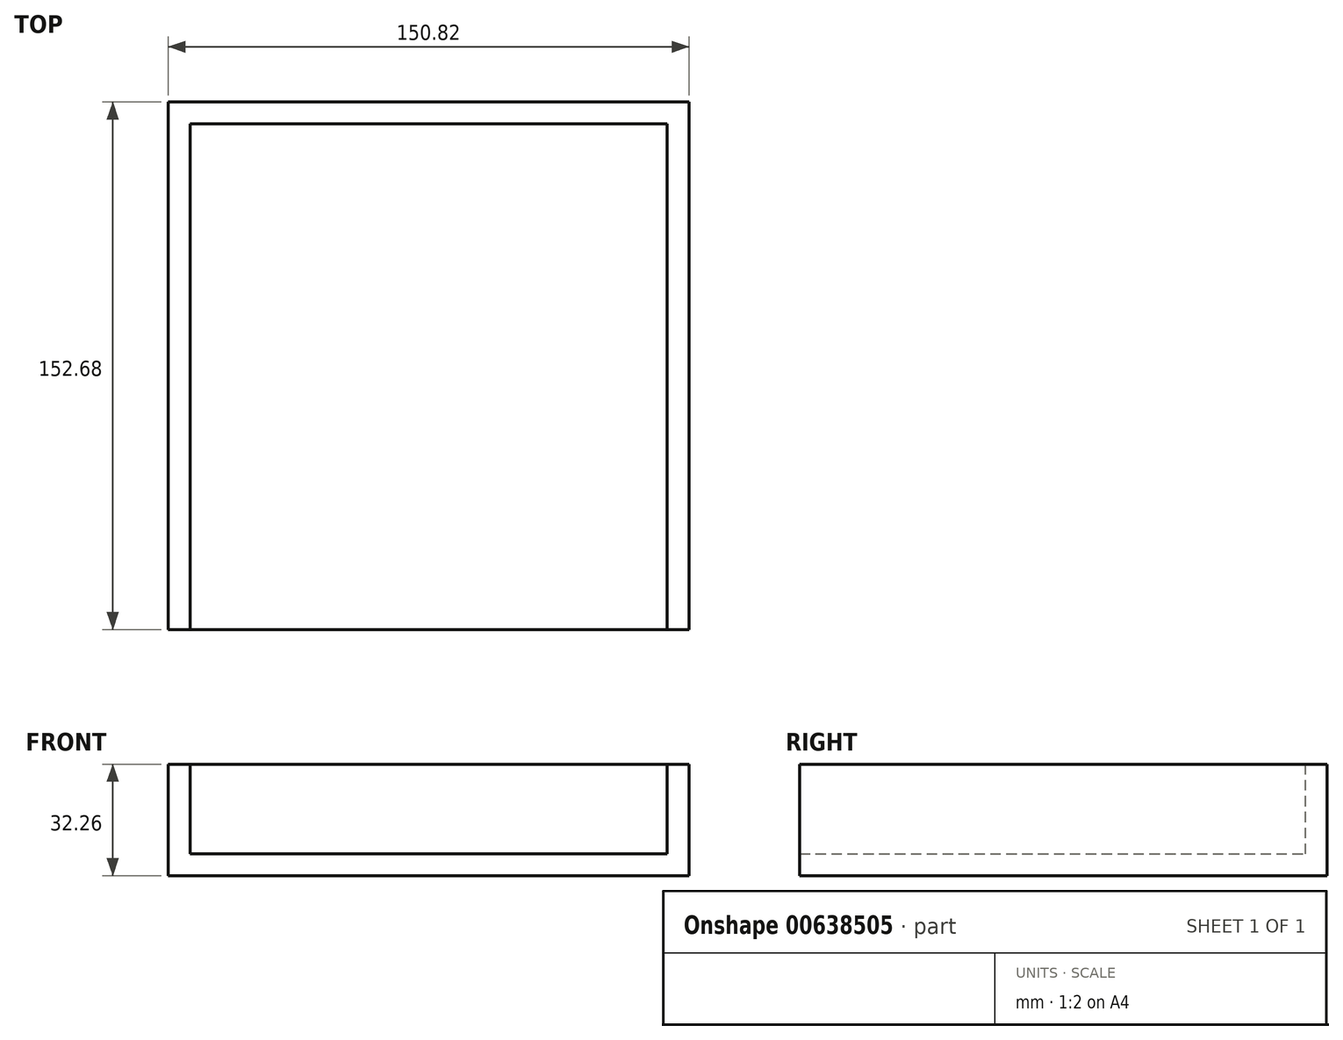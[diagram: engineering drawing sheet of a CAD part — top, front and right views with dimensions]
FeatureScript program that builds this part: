
annotation { "Feature Type Name" : "Feature", "Feature Type Description" : "" }
export const myFeature = defineFeature(function(context is Context, id is Id, definition is map)
    precondition{}
    {
        {
            var Q0;
            Q0=qCreatedBy(makeId("Top.planeOp"),FACE);
            var sketch = newSketch(context, id + "F0", { "sketchPlane" : qUnion([Q0])});
            skLineSegment(sketch, "E0.bottom", {"start": v(75.41, -76.34) * mm, "end": v(-75.41, -76.34) * mm});
            skLineSegment(sketch, "E0.top", {"start": v(75.41, 76.34) * mm, "end": v(-75.41, 76.34) * mm});
            skLineSegment(sketch, "E0.left", {"start": v(75.41, -76.34) * mm, "end": v(75.41, 76.34) * mm});
            skLineSegment(sketch, "E0.right", {"start": v(-75.41, -76.34) * mm, "end": v(-75.41, 76.34) * mm});
            skPoint(sketch, "E0.middle", {"position": v(0, 0) * mm});
            skSolve(sketch);
        }
        {
            var Q0;
            Q0=makeQuery(id+"F0.imprint","IMPRINT",FACE,{"disambiguationData":[TD([[makeQuery(id+"F0.imprint","IMPRINT",EDGE,{"derivedFrom":sQuery(id+"F0.wireOp",EDGE,"E0.bottom")}),-1.0]])]});
            extrude(context, id + "F1", {"entities" : qUnion([Q0]), "depth" : 32.26 * mm, "offsetDistance" : 25.4 * mm});
        }
        {
            var Q0;
            Q0=makeQuery(id+"F1.opExtrude","CAP_FACE",FACE,{"disambiguationData":[OSD([sQuery(id+"F0.wireOp",EDGE,"E0.bottom"),sQuery(id+"F0.wireOp",EDGE,"E0.top"),sQuery(id+"F0.wireOp",EDGE,"E0.left"),sQuery(id+"F0.wireOp",EDGE,"E0.right")])],"isStart":false});
            var Q1;
            Q1=makeQuery(id+"F1.opExtrude","SWEPT_FACE",FACE,{"disambiguationData":[OSD([sQuery(id+"F0.wireOp",EDGE,"E0.bottom")])]});
            shell(context, id + "F2", {"entities" : qUnion([Q0, Q1]), "thickness" : 6.35 * mm});
        }
    });
